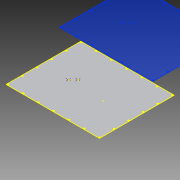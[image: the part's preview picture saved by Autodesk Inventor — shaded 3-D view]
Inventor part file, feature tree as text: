
AUTODESK INVENTOR PART (.ipt)
format: ipt  version: 2016 (Build 200138000, 138)  size: 171,520 bytes
history: native  units: in
note: dims shown in document units (in); Inventor stores cm internally (conversion verified against a paired STEP export)
features: sketch x4, hole x4, pattern_linear x4, extrude x1
ambient origin geometry x8: Origin, YZ Plane, XZ Plane, XY Plane, X Axis, Y Axis, Z Axis, Center Point
bodies: Solid1 (feature_tree)
feature tree (13):
  extrude  "Extrusion1"  Depth=8.0in
  sketch  "Sketch2"  dims[d4=0.06in d5=0.0in]
  hole  "Hole1"  [1 undecoded]
  pattern_linear  "Rectangular Pattern1"  Count1=7 Spacing1=1.635in
  pattern_linear  "Rectangular Pattern2"  Count1=5 Spacing1=1.562in
  hole  "Hole2"  [1 undecoded]
  pattern_linear  "Rectangular Pattern3"  Spacing1=0.0935in  [1 undecoded]
  pattern_linear  "Rectangular Pattern4"  Count1=5 Spacing1=1.562in
  sketch  "Sketch3"  dims[d6=0.096in d7=0.75in d8=0.16in d9=0.25in d10=0.5635in d11=1.0in d12=0.8108in d13=0.0935in]
  sketch  "Sketch6"  dims[d14=0.0935in d15=2.7559in d17=1.635in d18=1.9685in d20=1.562in d21=0.0935in d22=0.0935in d23=0.096in d24=0.75in d25=0.16in d26=0.25in d27=0.5635in d28=1.0in d29=0.8108in d30=1.9685in d32=1.562in d33=2.7559in d35=1.635in d36=0.128in d37=0.75in d38=0.232in d39=0.25in d40=0.5635in d41=0.06in d42=0.8108in d43=0.128in d44=0.75in d45=0.232in d46=0.25in d47=0.5635in d48=1.0in d49=0.8108in]
  hole  "Hole3"  [1 undecoded]
  hole  "Hole4"  [1 undecoded]
  sketch  "Sketch1"  dims[d0=10.0in d3=8.0in]
note: 5 required parameter values undecoded (feature->parameter linkage not recoverable at this tier; creation-order binding heuristic only, values carry confidence <= 0.55)
